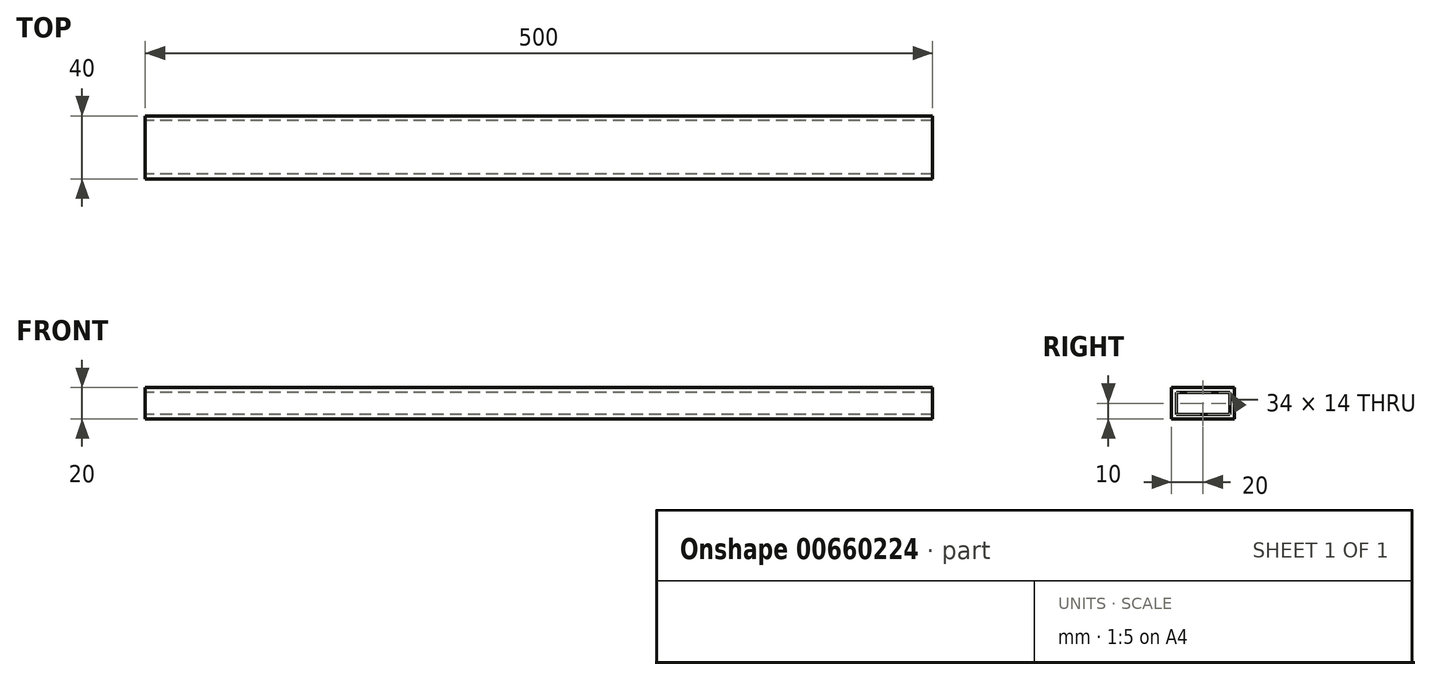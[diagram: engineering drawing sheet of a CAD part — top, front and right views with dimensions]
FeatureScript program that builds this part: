
annotation { "Feature Type Name" : "Feature", "Feature Type Description" : "" }
export const myFeature = defineFeature(function(context is Context, id is Id, definition is map)
    precondition{}
    {
        {
            var Q0;
            Q0=qCreatedBy(makeId("Right.planeOp"),FACE);
            var sketch = newSketch(context, id + "F0", { "sketchPlane" : qUnion([Q0])});
            skLineSegment(sketch, "E0.bottom", {"start": v(-20, 10) * mm, "end": v(20, 10) * mm});
            skLineSegment(sketch, "E0.top", {"start": v(-20, -10) * mm, "end": v(20, -10) * mm});
            skLineSegment(sketch, "E0.left", {"start": v(-20, 10) * mm, "end": v(-20, -10) * mm});
            skLineSegment(sketch, "E0.right", {"start": v(20, 10) * mm, "end": v(20, -10) * mm});
            skLineSegment(sketch, "E1.bottom", {"start": v(-17, 7) * mm, "end": v(17, 7) * mm});
            skLineSegment(sketch, "E1.top", {"start": v(-17, -7) * mm, "end": v(17, -7) * mm});
            skLineSegment(sketch, "E1.left", {"start": v(-17, 7) * mm, "end": v(-17, -7) * mm});
            skLineSegment(sketch, "E1.right", {"start": v(17, 7) * mm, "end": v(17, -7) * mm});
            skSolve(sketch);
        }
        {
            var Q0;
            Q0=makeQuery(id+"F0.imprint","IMPRINT",FACE,{"disambiguationData":[TD([[makeQuery(id+"F0.imprint","IMPRINT",EDGE,{"derivedFrom":sQuery(id+"F0.wireOp",EDGE,"E0.bottom")}),-1.0]])]});
            extrude(context, id + "F1", {"entities" : qUnion([Q0]), "endBound" : BoundingType.SYMMETRIC, "depth" : 500 * mm, "offsetDistance" : 25 * mm});
        }
    });
